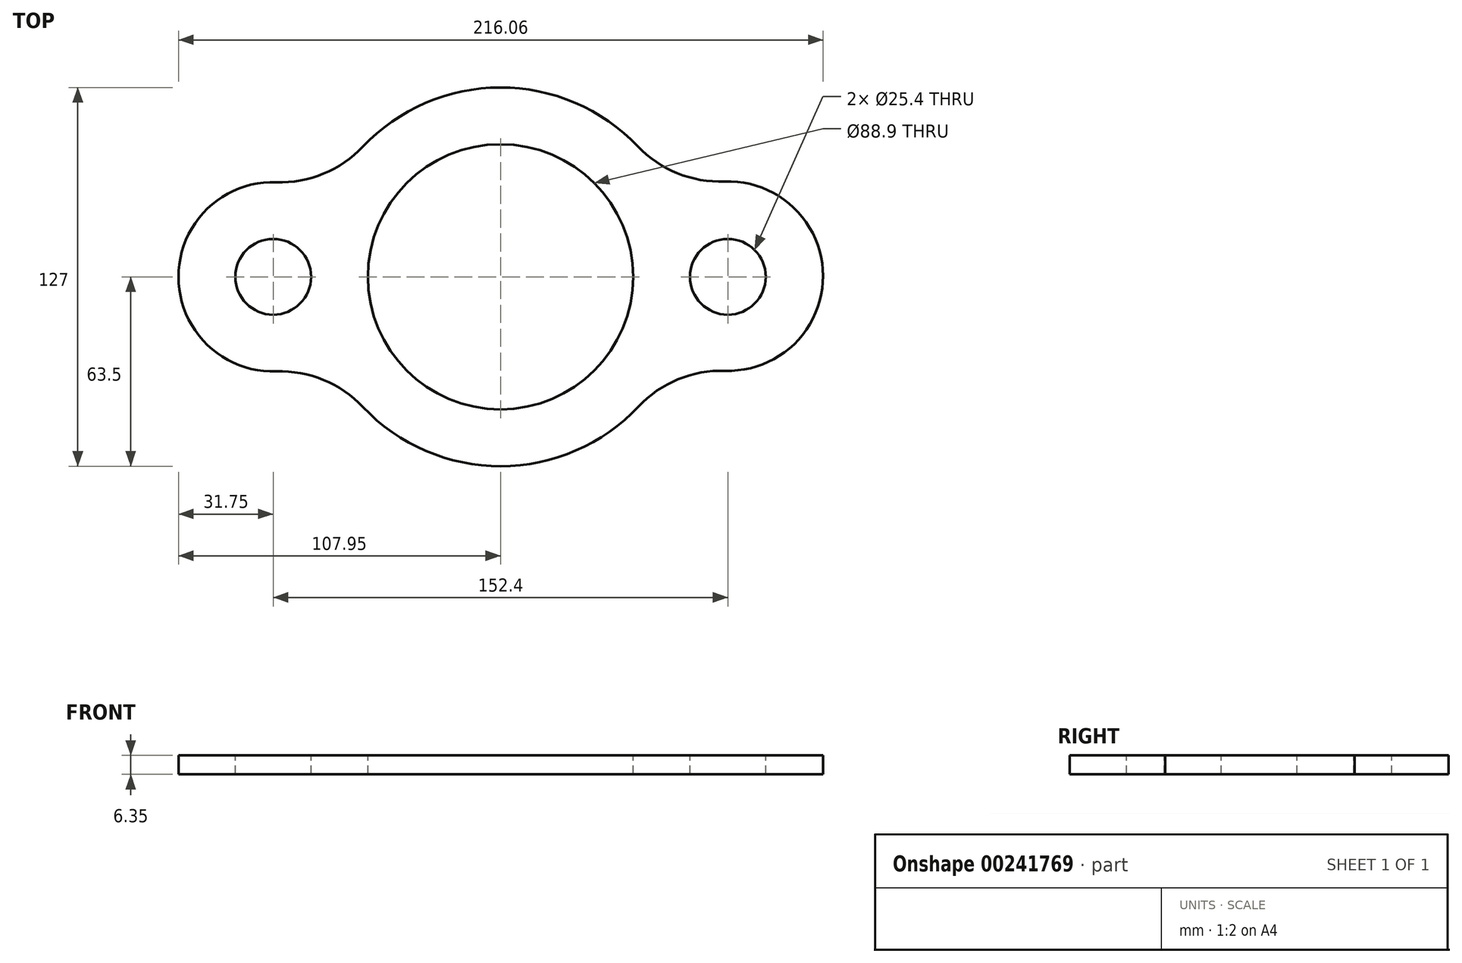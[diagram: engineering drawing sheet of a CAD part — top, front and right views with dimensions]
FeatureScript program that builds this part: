
annotation { "Feature Type Name" : "Feature", "Feature Type Description" : "" }
export const myFeature = defineFeature(function(context is Context, id is Id, definition is map)
    precondition{}
    {
        {
            var Q0;
            Q0=qCreatedBy(makeId("Top.planeOp"),FACE);
            var sketch = newSketch(context, id + "F0", { "sketchPlane" : qUnion([Q0])});
            skCircle(sketch, "E0", {"center": v(0, 0) * mm, "radius": 44.45 * mm});
            skCircle(sketch, "E1", {"center": v(-76.2, 0) * mm, "radius": 12.7 * mm});
            skCircle(sketch, "E2", {"center": v(76.2, 0) * mm, "radius": 12.7 * mm});
            skLineSegment(sketch, "E3", {"start": v(-76.2, 0) * mm, "end": v(0, 0) * mm, "construction": true});
            skLineSegment(sketch, "E4", {"start": v(-76.2, 0) * mm, "end": v(76.2, 0) * mm, "construction": true});
            skLineSegment(sketch, "E5", {"start": v(0, 0) * mm, "end": v(0, -76.09) * mm, "construction": true});
            skLineSegment(sketch, "E6", {"start": v(-76.2, 0) * mm, "end": v(-76.2, -31.55) * mm});
            skArc(sketch, "E7", {"start": v(-75.12, 31.73) * mm, "mid": v(-107.95, 0) * mm, "end": v(-75.12, -31.73) * mm});
            skArc(sketch, "E8", {"start": v(-46.14, -43.63) * mm, "mid": v(0.1, -63.5) * mm, "end": v(46.27, -43.49) * mm});
            skArc(sketch, "E9.filletArc", {"start": v(-75.12, 31.73) * mm, "mid": v(-59.35, 34.56) * mm, "end": v(-46.14, 43.63) * mm});
            skArc(sketch, "E10", {"start": v(75.3, -31.5) * mm, "mid": v(108.1, 0.32) * mm, "end": v(75.11, 31.95) * mm});
            skArc(sketch, "E11.trimOffspring", {"start": v(46, 43.77) * mm, "mid": v(-0.1, 63.5) * mm, "end": v(-46.14, 43.63) * mm});
            skArc(sketch, "E12.filletArc", {"start": v(-46.14, -43.63) * mm, "mid": v(-59.35, -34.56) * mm, "end": v(-75.12, -31.73) * mm});
            skArc(sketch, "E13.filletArc", {"start": v(75.3, -31.5) * mm, "mid": v(59.5, -34.37) * mm, "end": v(46.27, -43.49) * mm});
            skArc(sketch, "E14.filletArc", {"start": v(46, 43.77) * mm, "mid": v(59.29, 34.72) * mm, "end": v(75.11, 31.95) * mm});
            skSolve(sketch);
        }
        {
            var Q0;
            Q0 = qSketchRegion(id + "F0", true);
            extrude(context, id + "F1", {"entities" : qUnion([Q0]), "oppositeDirection" : true, "depth" : 6.35 * mm});
        }
    });
